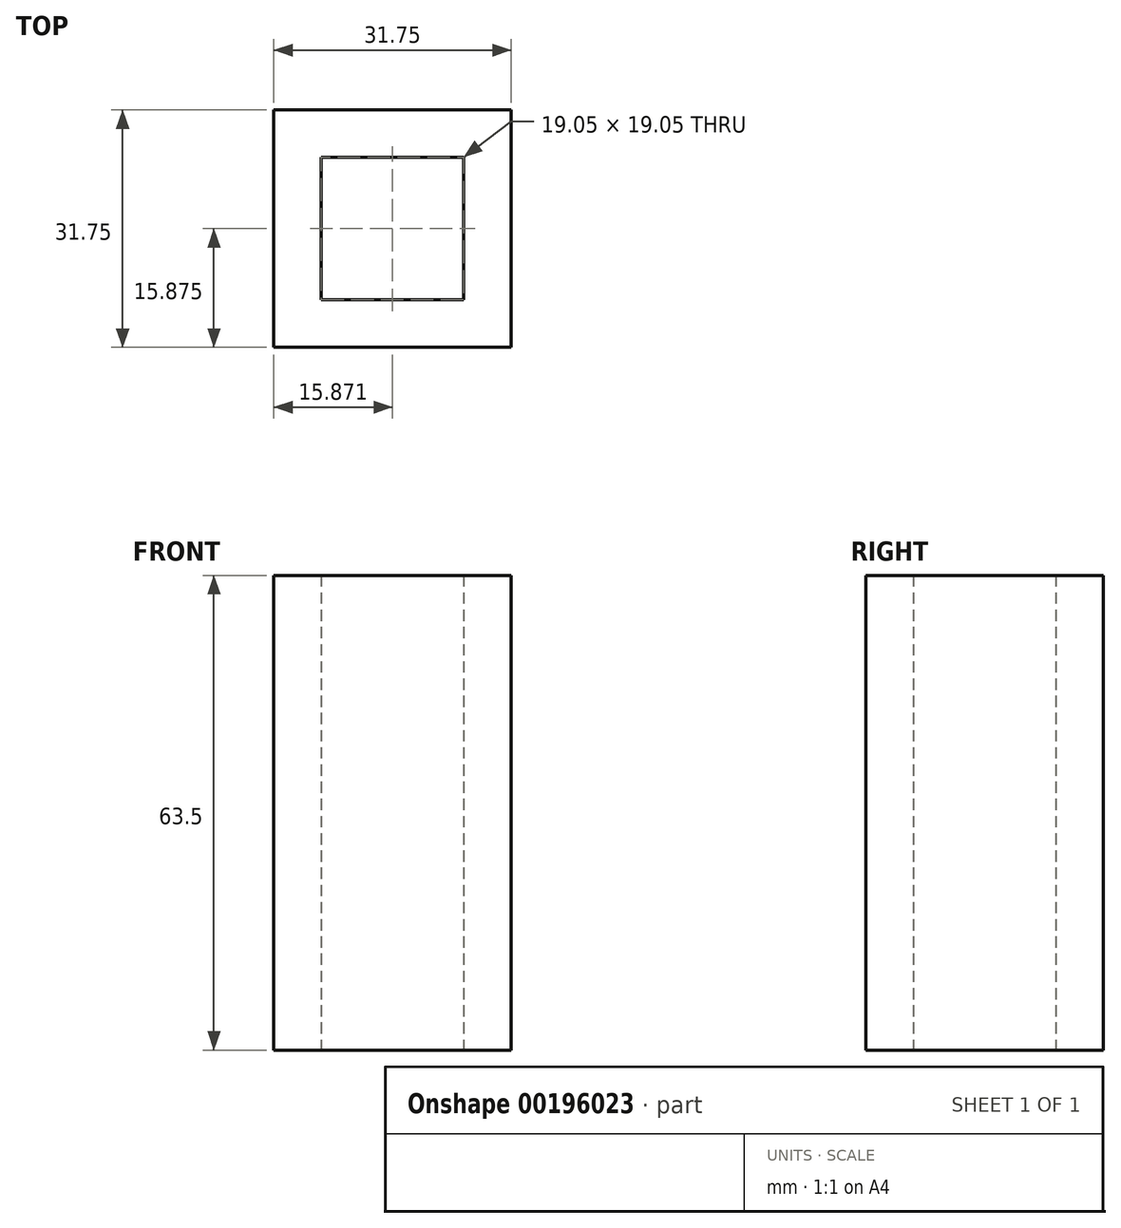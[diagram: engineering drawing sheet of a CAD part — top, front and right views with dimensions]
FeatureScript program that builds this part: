
annotation { "Feature Type Name" : "Feature", "Feature Type Description" : "" }
export const myFeature = defineFeature(function(context is Context, id is Id, definition is map)
    precondition{}
    {
        {
            var Q0;
            Q0=qCreatedBy(makeId("Top.planeOp"),FACE);
            var sketch = newSketch(context, id + "F0", { "sketchPlane" : qUnion([Q0])});
            skLineSegment(sketch, "E0.bottom", {"start": v(-12.48, 17.92) * mm, "end": v(19.27, 17.92) * mm});
            skLineSegment(sketch, "E0.top", {"start": v(-12.48, -13.83) * mm, "end": v(19.27, -13.83) * mm});
            skLineSegment(sketch, "E0.left", {"start": v(-12.48, 17.92) * mm, "end": v(-12.48, -13.83) * mm});
            skLineSegment(sketch, "E0.right", {"start": v(19.27, 17.92) * mm, "end": v(19.27, -13.83) * mm});
            skLineSegment(sketch, "E1.0", {"start": v(-6.13, 11.57) * mm, "end": v(12.92, 11.57) * mm});
            skLineSegment(sketch, "E1.1", {"start": v(-6.13, 11.57) * mm, "end": v(-6.13, -7.48) * mm});
            skLineSegment(sketch, "E1.2", {"start": v(-6.13, -7.48) * mm, "end": v(12.92, -7.48) * mm});
            skLineSegment(sketch, "E1.3", {"start": v(12.92, 11.57) * mm, "end": v(12.92, -7.48) * mm});
            skSolve(sketch);
        }
        {
            var Q0;
            Q0=makeQuery(id+"F0.imprint","IMPRINT",FACE,{"disambiguationData":[TD([[makeQuery(id+"F0.imprint","IMPRINT",EDGE,{"derivedFrom":sQuery(id+"F0.wireOp",EDGE,"E0.bottom")}),-1.0]])]});
            extrude(context, id + "F1", {"entities" : qUnion([Q0]), "depth" : 63.5 * mm});
        }
    });
